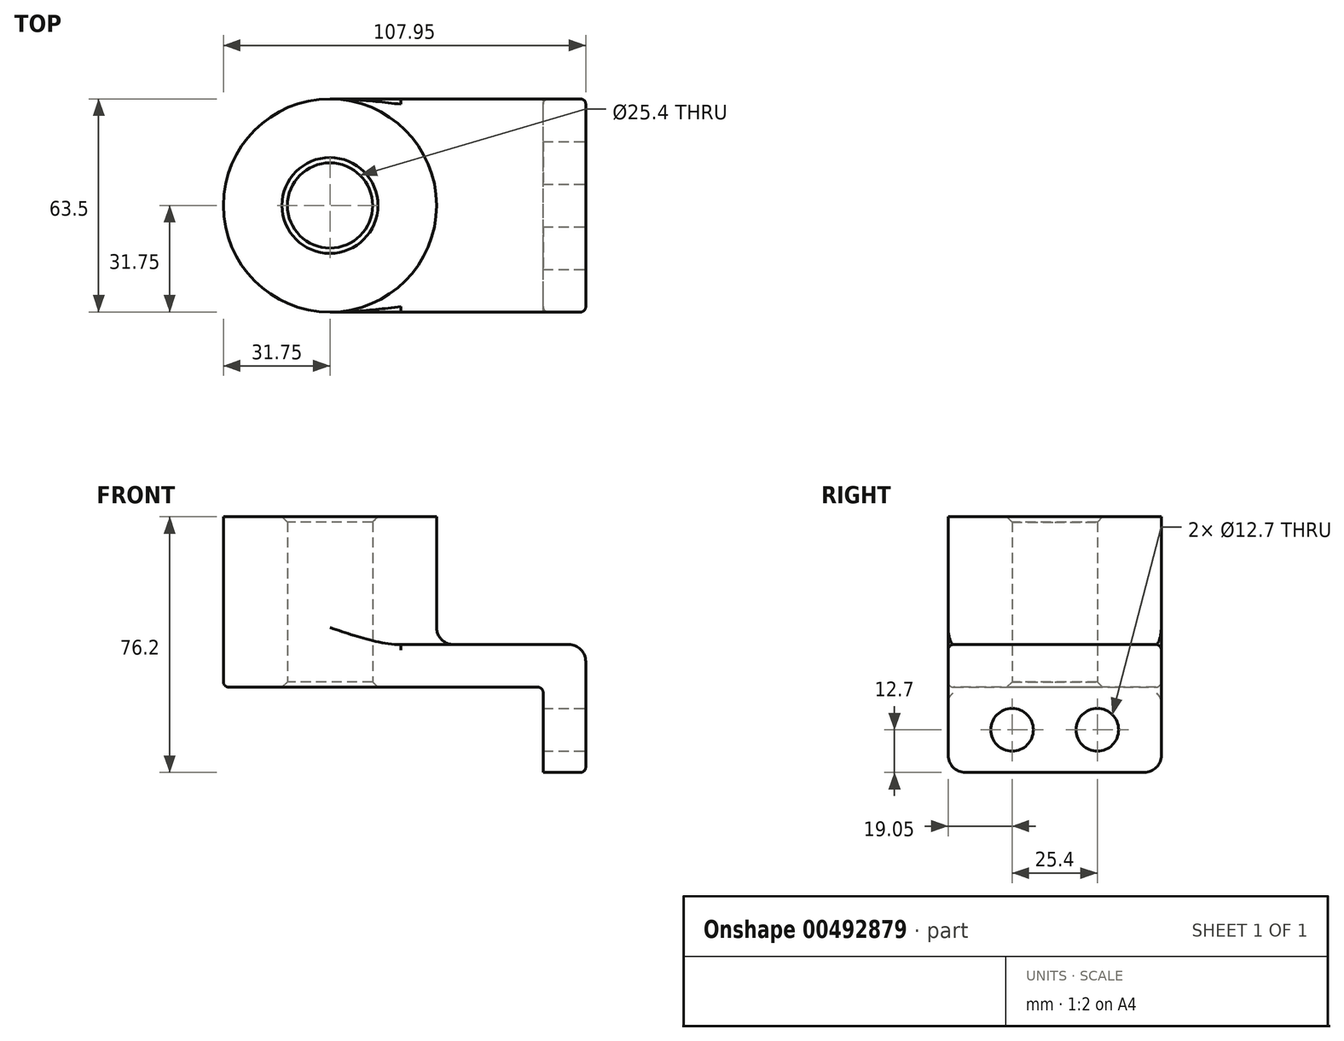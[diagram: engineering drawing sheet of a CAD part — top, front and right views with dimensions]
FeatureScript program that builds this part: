
annotation { "Feature Type Name" : "Feature", "Feature Type Description" : "" }
export const myFeature = defineFeature(function(context is Context, id is Id, definition is map)
    precondition{}
    {
        {
            var Q0;
            Q0=qCreatedBy(makeId("Top.planeOp"),FACE);
            var sketch = newSketch(context, id + "F0", { "sketchPlane" : qUnion([Q0])});
            skLineSegment(sketch, "E0.bottom", {"start": v(38.1, -31.75) * mm, "end": v(-38.1, -31.75) * mm});
            skLineSegment(sketch, "E0.top", {"start": v(38.1, 31.75) * mm, "end": v(-38.1, 31.75) * mm});
            skLineSegment(sketch, "E0.left", {"start": v(38.1, -31.75) * mm, "end": v(38.1, 31.75) * mm});
            skLineSegment(sketch, "E0.right", {"start": v(-38.1, -31.75) * mm, "end": v(-38.1, 31.75) * mm});
            skPoint(sketch, "E0.middle", {"position": v(0, 0) * mm});
            skCircle(sketch, "E1", {"center": v(-38.1, 0) * mm, "radius": 31.75 * mm});
            skCircle(sketch, "E2", {"center": v(-38.1, 0) * mm, "radius": 12.7 * mm});
            skSolve(sketch);
        }
        {
            var Q0;
            Q0 = qSketchRegion(id + "F0", true);
            extrude(context, id + "F1", {"entities" : qUnion([Q0]), "depth" : 12.7 * mm});
        }
        {
            var Q0;
            {var subQ1=sQuery(id+"F0.wireOp",EDGE,"E0.right");var subQ3=sQuery(id+"F0.wireOp",EDGE,"E2");var subQ4=makeQuery(id+"F0.imprint","INTERSECT",VERTEX,{"disambiguationData":[OD(0.0)],"derivedFrom":[subQ1,subQ3]});Q0=makeQuery(id+"F0.imprint","IMPRINT",FACE,{"disambiguationData":[TD([[makeQuery(id+"F0.imprint","IMPRINT",EDGE,{"disambiguationData":[TD([[subQ4,1.0]])],"derivedFrom":subQ3}),-1.0]])]});}
            var Q1;
            {var subQ1=sQuery(id+"F0.wireOp",EDGE,"E0.right");var subQ3=sQuery(id+"F0.wireOp",EDGE,"E2");var subQ4=makeQuery(id+"F0.imprint","INTERSECT",VERTEX,{"disambiguationData":[OD(0.0)],"derivedFrom":[subQ1,subQ3]});Q1=makeQuery(id+"F0.imprint","IMPRINT",FACE,{"disambiguationData":[TD([[makeQuery(id+"F0.imprint","IMPRINT",EDGE,{"disambiguationData":[TD([[subQ4,-1.0]])],"derivedFrom":subQ3}),-1.0]])]});}
            extrude(context, id + "F2", {"entities" : qUnion([Q0, Q1]), "operationType" : NewBodyOperationType.ADD, "depth" : 50.8 * mm});
        }
        {
            var Q0;
            Q0=makeQuery(id+"F1.opExtrude","SWEPT_FACE",FACE,{"disambiguationData":[OSD([sQuery(id+"F0.wireOp",EDGE,"E0.left")])]});
            var sketch = newSketch(context, id + "F3", { "sketchPlane" : qUnion([Q0])});
            skLineSegment(sketch, "E3.bottom", {"start": v(-31.75, 12.7) * mm, "end": v(31.75, 12.7) * mm});
            skLineSegment(sketch, "E3.top", {"start": v(-31.75, -25.4) * mm, "end": v(31.75, -25.4) * mm});
            skLineSegment(sketch, "E3.left", {"start": v(-31.75, 12.7) * mm, "end": v(-31.75, -25.4) * mm});
            skLineSegment(sketch, "E3.right", {"start": v(31.75, 12.7) * mm, "end": v(31.75, -25.4) * mm});
            skLineSegment(sketch, "E4", {"start": v(0, 0) * mm, "end": v(0, -25.4) * mm});
            skCircle(sketch, "E5", {"center": v(-12.7, -12.7) * mm, "radius": 6.35 * mm});
            skCircle(sketch, "E6.MirrorC", {"center": v(12.7, -12.7) * mm, "radius": 6.35 * mm});
            skSolve(sketch);
        }
        {
            var Q0;
            Q0 = qSketchRegion(id + "F3", true);
            extrude(context, id + "F4", {"entities" : qUnion([Q0]), "operationType" : NewBodyOperationType.ADD, "oppositeDirection" : true, "depth" : 12.7 * mm});
        }
        {
            var Q0;
            {var subQ0=sQuery(id+"F0.wireOp",EDGE,"E1");Q0=makeQuery(id+"F2.boolean.opBoolean","INTERSECT",EDGE,{"derivedFrom":[makeQuery(id+"F1.opExtrude","CAP_FACE",FACE,{"disambiguationData":[OSD([sQuery(id+"F0.wireOp",EDGE,"E0.bottom"),sQuery(id+"F0.wireOp",EDGE,"E0.top"),sQuery(id+"F0.wireOp",EDGE,"E0.left"),subQ0,sQuery(id+"F0.wireOp",EDGE,"E2")])],"isStart":false}),makeQuery(id+"F2.opExtrude","SWEPT_FACE",FACE,{"disambiguationData":[OSD([subQ0])]})]});}
            var Q1;
            Q1=makeQuery(id+"F4.opExtrude","SWEPT_EDGE",EDGE,{"disambiguationData":[OSD([sQuery(id+"F3.wireOp",EDGE,"E3.top"),sQuery(id+"F3.wireOp",EDGE,"E3.left")])]});
            var Q2;
            Q2=makeQuery(id+"F4.opExtrude","SWEPT_EDGE",EDGE,{"disambiguationData":[OSD([sQuery(id+"F3.wireOp",EDGE,"E3.top"),sQuery(id+"F3.wireOp",EDGE,"E3.right")])]});
            var Q3;
            Q3=makeQuery(id+"F1.opExtrude","CAP_EDGE",EDGE,{"disambiguationData":[OSD([sQuery(id+"F0.wireOp",EDGE,"E0.left")])],"isStart":false});
            fillet(context, id + "F5", {"entities" : qUnion([Q0, Q1, Q2, Q3]), "radius" : 5.08 * mm, "tangentPropagation" : true, "allowEdgeOverflow" : false});
        }
        {
            var Q0;
            Q0=makeQuery(id+"F1.opExtrude","CAP_EDGE",EDGE,{"disambiguationData":[OSD([sQuery(id+"F0.wireOp",EDGE,"E0.bottom")])],"isStart":false});
            var Q1;
            Q1=makeQuery(id+"F1.opExtrude","CAP_EDGE",EDGE,{"disambiguationData":[OSD([sQuery(id+"F0.wireOp",EDGE,"E0.bottom")])],"isStart":true});
            var Q2;
            Q2=makeQuery(id+"F4.boolean.opBoolean","INTERSECT",EDGE,{"derivedFrom":[makeQuery(id+"F1.opExtrude","CAP_FACE",FACE,{"disambiguationData":[OSD([sQuery(id+"F0.wireOp",EDGE,"E0.bottom"),sQuery(id+"F0.wireOp",EDGE,"E0.top"),sQuery(id+"F0.wireOp",EDGE,"E0.left"),sQuery(id+"F0.wireOp",EDGE,"E1"),sQuery(id+"F0.wireOp",EDGE,"E2")])],"isStart":true}),makeQuery(id+"F4.opExtrude","CAP_FACE",FACE,{"disambiguationData":[OSD([sQuery(id+"F3.wireOp",EDGE,"E3.bottom"),sQuery(id+"F3.wireOp",EDGE,"E3.top"),sQuery(id+"F3.wireOp",EDGE,"E3.left"),sQuery(id+"F3.wireOp",EDGE,"E3.right"),sQuery(id+"F3.wireOp",EDGE,"E5"),sQuery(id+"F3.wireOp",EDGE,"E6.MirrorC")])],"isStart":false})]});
            fillet(context, id + "F6", {"entities" : qUnion([Q0, Q1, Q2]), "radius" : 1.59 * mm, "tangentPropagation" : true, "allowEdgeOverflow" : false});
        }
        {
            var Q0;
            {var subQ0=sQuery(id+"F0.wireOp",EDGE,"E2");Q0=makeQuery(id+"F2.boolean.opBoolean","MERGE",FACE,{"derivedFrom":[makeQuery(id+"F1.opExtrude","SWEPT_FACE",FACE,{"disambiguationData":[OSD([subQ0])]}),makeQuery(id+"F2.opExtrude","SWEPT_FACE",FACE,{"disambiguationData":[OSD([subQ0])]})]});}
            chamfer(context, id + "F7", {"entities" : qUnion([Q0]), "width" : 1.59 * mm, "tangentPropagation" : true});
        }
    });
